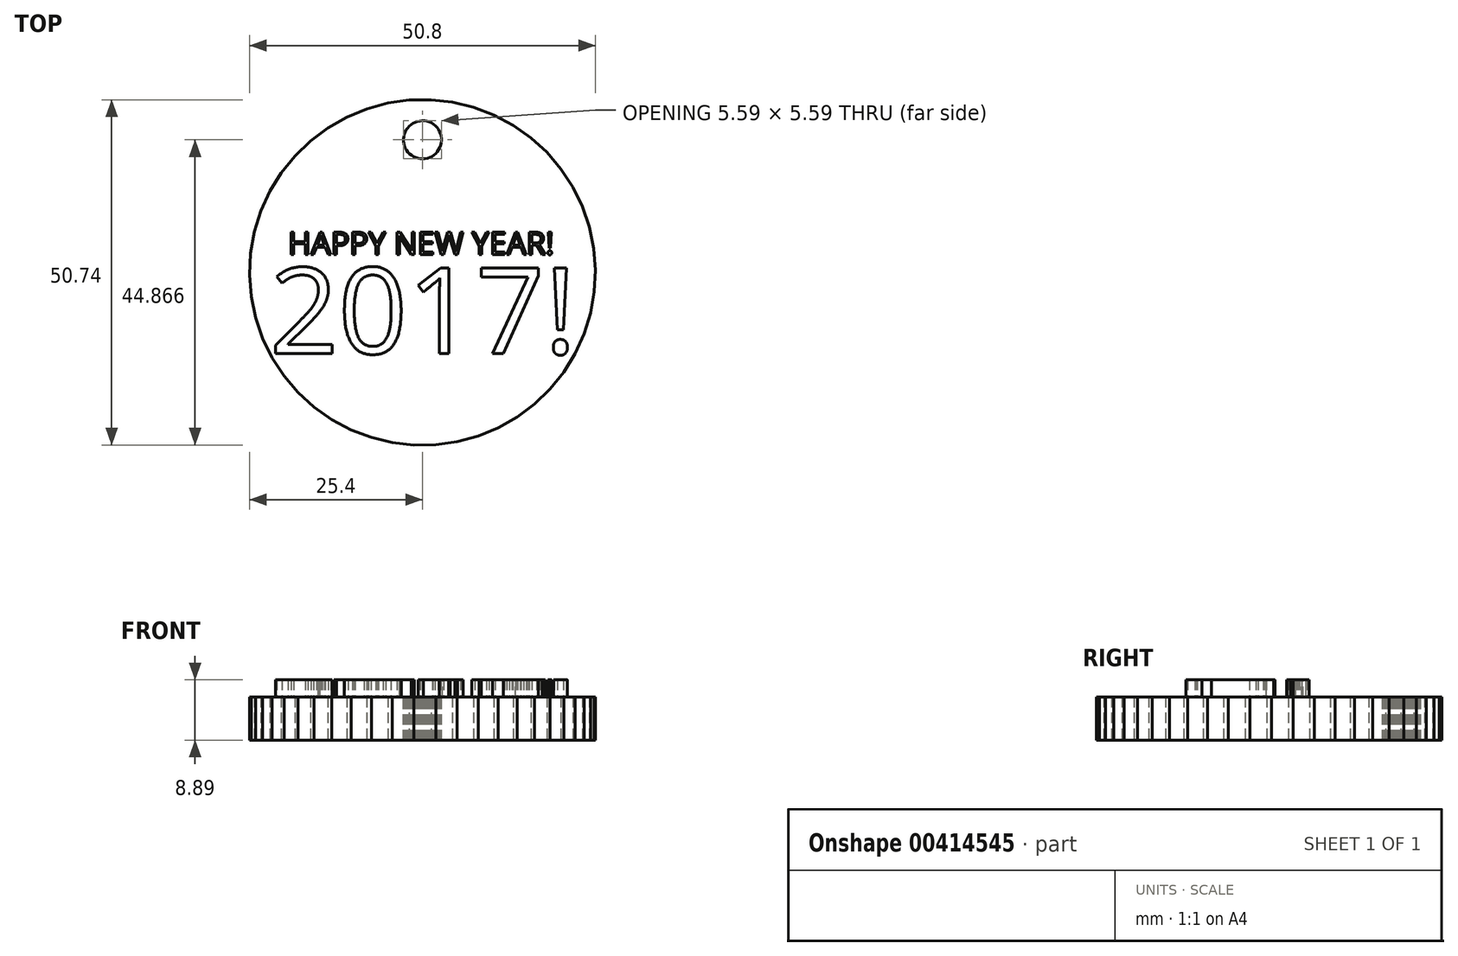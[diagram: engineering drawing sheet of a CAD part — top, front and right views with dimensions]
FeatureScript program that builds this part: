
annotation { "Feature Type Name" : "Feature", "Feature Type Description" : "" }
export const myFeature = defineFeature(function(context is Context, id is Id, definition is map)
    precondition{}
    {
        {
            var Q0;
            Q0=qCreatedBy(makeId("Top.planeOp"),FACE);
            var sketch = newSketch(context, id + "F0", { "sketchPlane" : qUnion([Q0])});
            skCircle(sketch, "E0.cCircle", {"center": v(0, 0) * mm, "radius": 25.4 * mm, "construction": true});
            skLineSegment(sketch, "E0.0", {"start": v(22.09, 12.54) * mm, "end": v(23.48, 9.68) * mm});
            skLineSegment(sketch, "E0.1", {"start": v(23.48, 9.68) * mm, "end": v(24.51, 6.66) * mm});
            skLineSegment(sketch, "E0.2", {"start": v(24.51, 6.66) * mm, "end": v(25.15, 3.53) * mm});
            skLineSegment(sketch, "E0.3", {"start": v(25.15, 3.53) * mm, "end": v(25.4, 0.35) * mm});
            skLineSegment(sketch, "E0.4", {"start": v(25.4, 0.35) * mm, "end": v(25.24, -2.83) * mm});
            skLineSegment(sketch, "E0.5", {"start": v(25.24, -2.83) * mm, "end": v(24.69, -5.98) * mm});
            skLineSegment(sketch, "E0.6", {"start": v(24.69, -5.98) * mm, "end": v(23.74, -9.02) * mm});
            skLineSegment(sketch, "E0.7", {"start": v(23.74, -9.02) * mm, "end": v(22.43, -11.93) * mm});
            skLineSegment(sketch, "E0.8", {"start": v(22.43, -11.93) * mm, "end": v(20.75, -14.64) * mm});
            skLineSegment(sketch, "E0.9", {"start": v(20.75, -14.64) * mm, "end": v(18.75, -17.13) * mm});
            skLineSegment(sketch, "E0.10", {"start": v(18.75, -17.13) * mm, "end": v(16.46, -19.34) * mm});
            skLineSegment(sketch, "E0.11", {"start": v(16.46, -19.34) * mm, "end": v(13.9, -21.26) * mm});
            skLineSegment(sketch, "E0.12", {"start": v(13.9, -21.26) * mm, "end": v(11.13, -22.83) * mm});
            skLineSegment(sketch, "E0.13", {"start": v(11.13, -22.83) * mm, "end": v(8.18, -24.05) * mm});
            skLineSegment(sketch, "E0.14", {"start": v(8.18, -24.05) * mm, "end": v(5.1, -24.88) * mm});
            skLineSegment(sketch, "E0.15", {"start": v(5.1, -24.88) * mm, "end": v(1.95, -25.33) * mm});
            skLineSegment(sketch, "E0.16", {"start": v(1.95, -25.33) * mm, "end": v(-1.24, -25.37) * mm});
            skLineSegment(sketch, "E0.17", {"start": v(-1.24, -25.37) * mm, "end": v(-4.41, -25.01) * mm});
            skLineSegment(sketch, "E0.18", {"start": v(-4.41, -25.01) * mm, "end": v(-7.51, -24.26) * mm});
            skLineSegment(sketch, "E0.19", {"start": v(-7.51, -24.26) * mm, "end": v(-10.5, -23.13) * mm});
            skLineSegment(sketch, "E0.20", {"start": v(-10.5, -23.13) * mm, "end": v(-13.31, -21.63) * mm});
            skLineSegment(sketch, "E0.21", {"start": v(-13.31, -21.63) * mm, "end": v(-15.92, -19.8) * mm});
            skLineSegment(sketch, "E0.22", {"start": v(-15.92, -19.8) * mm, "end": v(-18.27, -17.64) * mm});
            skLineSegment(sketch, "E0.23", {"start": v(-18.27, -17.64) * mm, "end": v(-20.34, -15.21) * mm});
            skLineSegment(sketch, "E0.24", {"start": v(-20.34, -15.21) * mm, "end": v(-22.09, -12.54) * mm});
            skLineSegment(sketch, "E0.25", {"start": v(-22.09, -12.54) * mm, "end": v(-23.48, -9.68) * mm});
            skLineSegment(sketch, "E0.26", {"start": v(-23.48, -9.68) * mm, "end": v(-24.51, -6.66) * mm});
            skLineSegment(sketch, "E0.27", {"start": v(-24.51, -6.66) * mm, "end": v(-25.15, -3.53) * mm});
            skLineSegment(sketch, "E0.28", {"start": v(-25.15, -3.53) * mm, "end": v(-25.4, -0.35) * mm});
            skLineSegment(sketch, "E0.29", {"start": v(-25.4, -0.35) * mm, "end": v(-25.24, 2.83) * mm});
            skLineSegment(sketch, "E0.30", {"start": v(-25.24, 2.83) * mm, "end": v(-24.69, 5.98) * mm});
            skLineSegment(sketch, "E0.31", {"start": v(-24.69, 5.98) * mm, "end": v(-23.74, 9.02) * mm});
            skLineSegment(sketch, "E0.32", {"start": v(-23.74, 9.02) * mm, "end": v(-22.43, 11.93) * mm});
            skLineSegment(sketch, "E0.33", {"start": v(-22.43, 11.93) * mm, "end": v(-20.75, 14.64) * mm});
            skLineSegment(sketch, "E0.34", {"start": v(-20.75, 14.64) * mm, "end": v(-18.75, 17.13) * mm});
            skLineSegment(sketch, "E0.35", {"start": v(-18.75, 17.13) * mm, "end": v(-16.46, 19.34) * mm});
            skLineSegment(sketch, "E0.36", {"start": v(-16.46, 19.34) * mm, "end": v(-13.9, 21.26) * mm});
            skLineSegment(sketch, "E0.37", {"start": v(-13.9, 21.26) * mm, "end": v(-11.13, 22.83) * mm});
            skLineSegment(sketch, "E0.38", {"start": v(-11.13, 22.83) * mm, "end": v(-8.18, 24.05) * mm});
            skLineSegment(sketch, "E0.39", {"start": v(-8.18, 24.05) * mm, "end": v(-5.1, 24.88) * mm});
            skLineSegment(sketch, "E0.40", {"start": v(-5.1, 24.88) * mm, "end": v(-1.95, 25.33) * mm});
            skLineSegment(sketch, "E0.41", {"start": v(-1.95, 25.33) * mm, "end": v(1.24, 25.37) * mm});
            skLineSegment(sketch, "E0.42", {"start": v(1.24, 25.37) * mm, "end": v(4.41, 25.01) * mm});
            skLineSegment(sketch, "E0.43", {"start": v(4.41, 25.01) * mm, "end": v(7.51, 24.26) * mm});
            skLineSegment(sketch, "E0.44", {"start": v(7.51, 24.26) * mm, "end": v(10.5, 23.13) * mm});
            skLineSegment(sketch, "E0.45", {"start": v(10.5, 23.13) * mm, "end": v(13.31, 21.63) * mm});
            skLineSegment(sketch, "E0.46", {"start": v(13.31, 21.63) * mm, "end": v(15.92, 19.8) * mm});
            skLineSegment(sketch, "E0.47", {"start": v(15.92, 19.8) * mm, "end": v(18.27, 17.64) * mm});
            skLineSegment(sketch, "E0.48", {"start": v(18.27, 17.64) * mm, "end": v(20.34, 15.21) * mm});
            skLineSegment(sketch, "E0.49", {"start": v(20.34, 15.21) * mm, "end": v(22.09, 12.54) * mm});
            skSolve(sketch);
        }
        {
            var Q0;
            Q0=makeQuery(id+"F0.imprint","IMPRINT",FACE,{"disambiguationData":[TD([[makeQuery(id+"F0.imprint","IMPRINT",EDGE,{"derivedFrom":sQuery(id+"F0.wireOp",EDGE,"E0.0")}),-1.0]])]});
            extrude(context, id + "F1", {"entities" : qUnion([Q0]), "depth" : 6.35 * mm});
        }
        {
            var Q0;
            Q0=makeQuery(id+"F1.opExtrude","CAP_FACE",FACE,{"disambiguationData":[OSD([sQuery(id+"F0.wireOp",EDGE,"E0.0"),sQuery(id+"F0.wireOp",EDGE,"E0.1"),sQuery(id+"F0.wireOp",EDGE,"E0.2"),sQuery(id+"F0.wireOp",EDGE,"E0.3"),sQuery(id+"F0.wireOp",EDGE,"E0.4"),sQuery(id+"F0.wireOp",EDGE,"E0.5"),sQuery(id+"F0.wireOp",EDGE,"E0.6"),sQuery(id+"F0.wireOp",EDGE,"E0.7"),sQuery(id+"F0.wireOp",EDGE,"E0.8"),sQuery(id+"F0.wireOp",EDGE,"E0.9"),sQuery(id+"F0.wireOp",EDGE,"E0.10"),sQuery(id+"F0.wireOp",EDGE,"E0.11"),sQuery(id+"F0.wireOp",EDGE,"E0.12"),sQuery(id+"F0.wireOp",EDGE,"E0.13"),sQuery(id+"F0.wireOp",EDGE,"E0.14"),sQuery(id+"F0.wireOp",EDGE,"E0.15"),sQuery(id+"F0.wireOp",EDGE,"E0.16"),sQuery(id+"F0.wireOp",EDGE,"E0.17"),sQuery(id+"F0.wireOp",EDGE,"E0.18"),sQuery(id+"F0.wireOp",EDGE,"E0.19"),sQuery(id+"F0.wireOp",EDGE,"E0.20"),sQuery(id+"F0.wireOp",EDGE,"E0.21"),sQuery(id+"F0.wireOp",EDGE,"E0.22"),sQuery(id+"F0.wireOp",EDGE,"E0.23"),sQuery(id+"F0.wireOp",EDGE,"E0.24"),sQuery(id+"F0.wireOp",EDGE,"E0.25"),sQuery(id+"F0.wireOp",EDGE,"E0.26"),sQuery(id+"F0.wireOp",EDGE,"E0.27"),sQuery(id+"F0.wireOp",EDGE,"E0.28"),sQuery(id+"F0.wireOp",EDGE,"E0.29"),sQuery(id+"F0.wireOp",EDGE,"E0.30"),sQuery(id+"F0.wireOp",EDGE,"E0.31"),sQuery(id+"F0.wireOp",EDGE,"E0.32"),sQuery(id+"F0.wireOp",EDGE,"E0.33"),sQuery(id+"F0.wireOp",EDGE,"E0.34"),sQuery(id+"F0.wireOp",EDGE,"E0.35"),sQuery(id+"F0.wireOp",EDGE,"E0.36"),sQuery(id+"F0.wireOp",EDGE,"E0.37"),sQuery(id+"F0.wireOp",EDGE,"E0.38"),sQuery(id+"F0.wireOp",EDGE,"E0.39"),sQuery(id+"F0.wireOp",EDGE,"E0.40"),sQuery(id+"F0.wireOp",EDGE,"E0.41"),sQuery(id+"F0.wireOp",EDGE,"E0.42"),sQuery(id+"F0.wireOp",EDGE,"E0.43"),sQuery(id+"F0.wireOp",EDGE,"E0.44"),sQuery(id+"F0.wireOp",EDGE,"E0.45"),sQuery(id+"F0.wireOp",EDGE,"E0.46"),sQuery(id+"F0.wireOp",EDGE,"E0.47"),sQuery(id+"F0.wireOp",EDGE,"E0.48"),sQuery(id+"F0.wireOp",EDGE,"E0.49")])],"isStart":false});
            var sketch = newSketch(context, id + "F2", { "sketchPlane" : qUnion([Q0])});
            skText(sketch, "E1", { "text": "2017!", "fontName": "OpenSans-Regular.ttf"});
            skPoint(sketch, "E2.firstSnap0", {"position": v(-23.08, 10.47) * mm});
            skText(sketch, "E3", { "text": "HAPPY NEW YEAR!", "fontName": "OpenSans-Regular.ttf"});
            skPoint(sketch, "E3.firstSnap0", {"position": v(-19.75, 15.89) * mm});
            const initialGuessF2  = {"E1": [-0.02243, -0.01193, 1, 0, 0.0127], "E3": [-0.01975, 0.00264, 1, 0, 0.0033]};
            skSetInitialGuess(sketch, initialGuessF2);
            skSolve(sketch);
        }
        {
            var Q0;
            Q0 = qSketchRegion(id + "F2", true);
            extrude(context, id + "F3", {"entities" : qUnion([Q0]), "operationType" : NewBodyOperationType.ADD, "depth" : 2.54 * mm});
        }
        {
            var Q0;
            {var subQ0=sQuery(id+"F0.wireOp",EDGE,"E0.44");var subQ1=sQuery(id+"F0.wireOp",EDGE,"E0.43");var subQ2=sQuery(id+"F0.wireOp",EDGE,"E0.42");var subQ3=sQuery(id+"F0.wireOp",EDGE,"E0.41");var subQ4=sQuery(id+"F0.wireOp",EDGE,"E0.40");var subQ5=sQuery(id+"F0.wireOp",EDGE,"E0.39");var subQ6=sQuery(id+"F0.wireOp",EDGE,"E0.38");var subQ7=sQuery(id+"F0.wireOp",EDGE,"E0.37");var subQ8=sQuery(id+"F0.wireOp",EDGE,"E0.27");var subQ9=sQuery(id+"F0.wireOp",EDGE,"E0.36");var subQ10=sQuery(id+"F0.wireOp",EDGE,"E0.26");var subQ11=sQuery(id+"F0.wireOp",EDGE,"E0.35");var subQ12=sQuery(id+"F0.wireOp",EDGE,"E0.34");var subQ13=sQuery(id+"F0.wireOp",EDGE,"E0.24");var subQ14=sQuery(id+"F0.wireOp",EDGE,"E0.33");var subQ15=sQuery(id+"F0.wireOp",EDGE,"E0.23");var subQ16=sQuery(id+"F0.wireOp",EDGE,"E0.32");var subQ17=sQuery(id+"F0.wireOp",EDGE,"E0.22");var subQ18=sQuery(id+"F0.wireOp",EDGE,"E0.31");var subQ19=sQuery(id+"F0.wireOp",EDGE,"E0.8");var subQ20=sQuery(id+"F0.wireOp",EDGE,"E0.7");var subQ21=sQuery(id+"F0.wireOp",EDGE,"E0.6");var subQ22=sQuery(id+"F0.wireOp",EDGE,"E0.5");var subQ23=sQuery(id+"F0.wireOp",EDGE,"E0.4");var subQ24=sQuery(id+"F0.wireOp",EDGE,"E0.9");var subQ25=sQuery(id+"F0.wireOp",EDGE,"E0.45");var subQ26=sQuery(id+"F0.wireOp",EDGE,"E0.0");var subQ27=sQuery(id+"F0.wireOp",EDGE,"E0.21");var subQ28=sQuery(id+"F0.wireOp",EDGE,"E0.30");var subQ29=sQuery(id+"F0.wireOp",EDGE,"E0.3");var subQ30=sQuery(id+"F0.wireOp",EDGE,"E0.1");var subQ31=sQuery(id+"F0.wireOp",EDGE,"E0.2");var subQ32=sQuery(id+"F0.wireOp",EDGE,"E0.10");var subQ33=sQuery(id+"F0.wireOp",EDGE,"E0.11");var subQ34=sQuery(id+"F0.wireOp",EDGE,"E0.12");var subQ35=sQuery(id+"F0.wireOp",EDGE,"E0.13");var subQ36=sQuery(id+"F0.wireOp",EDGE,"E0.14");var subQ37=sQuery(id+"F0.wireOp",EDGE,"E0.15");var subQ38=sQuery(id+"F0.wireOp",EDGE,"E0.16");var subQ39=sQuery(id+"F0.wireOp",EDGE,"E0.25");var subQ40=sQuery(id+"F0.wireOp",EDGE,"E0.47");var subQ41=sQuery(id+"F0.wireOp",EDGE,"E0.17");var subQ42=sQuery(id+"F0.wireOp",EDGE,"E0.18");var subQ43=sQuery(id+"F0.wireOp",EDGE,"E0.19");var subQ44=sQuery(id+"F0.wireOp",EDGE,"E0.28");var subQ45=sQuery(id+"F0.wireOp",EDGE,"E0.20");var subQ46=sQuery(id+"F0.wireOp",EDGE,"E0.29");var subQ47=sQuery(id+"F0.wireOp",EDGE,"E0.46");var subQ48=sQuery(id+"F0.wireOp",EDGE,"E0.48");var subQ49=sQuery(id+"F0.wireOp",EDGE,"E0.49");Q0=makeQuery(id+"F3.boolean.opBoolean","SPLIT",FACE,{"disambiguationData":[TD([makeQuery(id+"F1.opExtrude","SWEPT_FACE",FACE,{"disambiguationData":[OSD([subQ26])]})])],"derivedFrom":makeQuery(id+"F1.opExtrude","CAP_FACE",FACE,{"disambiguationData":[OSD([subQ26,subQ30,subQ31,subQ29,subQ23,subQ22,subQ21,subQ20,subQ19,subQ24,subQ32,subQ33,subQ34,subQ35,subQ36,subQ37,subQ38,subQ41,subQ42,subQ43,subQ45,subQ27,subQ17,subQ15,subQ13,subQ39,subQ10,subQ8,subQ44,subQ46,subQ28,subQ18,subQ16,subQ14,subQ12,subQ11,subQ9,subQ7,subQ6,subQ5,subQ4,subQ3,subQ2,subQ1,subQ0,subQ25,subQ47,subQ40,subQ48,subQ49])],"isStart":false})});}
            var sketch = newSketch(context, id + "F4", { "sketchPlane" : qUnion([Q0])});
            skCircle(sketch, "E4.cCircle", {"center": v(0, 19.5) * mm, "radius": 2.8 * mm, "construction": true});
            skLineSegment(sketch, "E4.0", {"start": v(2.34, 21.03) * mm, "end": v(2.51, 20.72) * mm});
            skLineSegment(sketch, "E4.1", {"start": v(2.51, 20.72) * mm, "end": v(2.65, 20.4) * mm});
            skLineSegment(sketch, "E4.2", {"start": v(2.65, 20.4) * mm, "end": v(2.74, 20.06) * mm});
            skLineSegment(sketch, "E4.3", {"start": v(2.74, 20.06) * mm, "end": v(2.79, 19.71) * mm});
            skLineSegment(sketch, "E4.4", {"start": v(2.79, 19.71) * mm, "end": v(2.8, 19.36) * mm});
            skLineSegment(sketch, "E4.5", {"start": v(2.8, 19.36) * mm, "end": v(2.75, 19.01) * mm});
            skLineSegment(sketch, "E4.6", {"start": v(2.75, 19.01) * mm, "end": v(2.67, 18.67) * mm});
            skLineSegment(sketch, "E4.7", {"start": v(2.67, 18.67) * mm, "end": v(2.55, 18.34) * mm});
            skLineSegment(sketch, "E4.8", {"start": v(2.55, 18.34) * mm, "end": v(2.38, 18.03) * mm});
            skLineSegment(sketch, "E4.9", {"start": v(2.38, 18.03) * mm, "end": v(2.18, 17.74) * mm});
            skLineSegment(sketch, "E4.10", {"start": v(2.18, 17.74) * mm, "end": v(1.94, 17.48) * mm});
            skLineSegment(sketch, "E4.11", {"start": v(1.94, 17.48) * mm, "end": v(1.68, 17.26) * mm});
            skLineSegment(sketch, "E4.12", {"start": v(1.68, 17.26) * mm, "end": v(1.38, 17.06) * mm});
            skLineSegment(sketch, "E4.13", {"start": v(1.38, 17.06) * mm, "end": v(1.07, 16.91) * mm});
            skLineSegment(sketch, "E4.14", {"start": v(1.07, 16.91) * mm, "end": v(0.73, 16.8) * mm});
            skLineSegment(sketch, "E4.15", {"start": v(0.73, 16.8) * mm, "end": v(0.39, 16.73) * mm});
            skLineSegment(sketch, "E4.16", {"start": v(0.39, 16.73) * mm, "end": v(0.04, 16.7) * mm});
            skLineSegment(sketch, "E4.17", {"start": v(0.04, 16.7) * mm, "end": v(-0.31, 16.72) * mm});
            skLineSegment(sketch, "E4.18", {"start": v(-0.31, 16.72) * mm, "end": v(-0.66, 16.78) * mm});
            skLineSegment(sketch, "E4.19", {"start": v(-0.66, 16.78) * mm, "end": v(-1, 16.88) * mm});
            skLineSegment(sketch, "E4.20", {"start": v(-1, 16.88) * mm, "end": v(-1.31, 17.03) * mm});
            skLineSegment(sketch, "E4.21", {"start": v(-1.31, 17.03) * mm, "end": v(-1.61, 17.21) * mm});
            skLineSegment(sketch, "E4.22", {"start": v(-1.61, 17.21) * mm, "end": v(-1.89, 17.43) * mm});
            skLineSegment(sketch, "E4.23", {"start": v(-1.89, 17.43) * mm, "end": v(-2.13, 17.68) * mm});
            skLineSegment(sketch, "E4.24", {"start": v(-2.13, 17.68) * mm, "end": v(-2.34, 17.96) * mm});
            skLineSegment(sketch, "E4.25", {"start": v(-2.34, 17.96) * mm, "end": v(-2.51, 18.27) * mm});
            skLineSegment(sketch, "E4.26", {"start": v(-2.51, 18.27) * mm, "end": v(-2.65, 18.6) * mm});
            skLineSegment(sketch, "E4.27", {"start": v(-2.65, 18.6) * mm, "end": v(-2.74, 18.93) * mm});
            skLineSegment(sketch, "E4.28", {"start": v(-2.74, 18.93) * mm, "end": v(-2.79, 19.28) * mm});
            skLineSegment(sketch, "E4.29", {"start": v(-2.79, 19.28) * mm, "end": v(-2.8, 19.63) * mm});
            skLineSegment(sketch, "E4.30", {"start": v(-2.8, 19.63) * mm, "end": v(-2.75, 19.98) * mm});
            skLineSegment(sketch, "E4.31", {"start": v(-2.75, 19.98) * mm, "end": v(-2.67, 20.32) * mm});
            skLineSegment(sketch, "E4.32", {"start": v(-2.67, 20.32) * mm, "end": v(-2.55, 20.65) * mm});
            skLineSegment(sketch, "E4.33", {"start": v(-2.55, 20.65) * mm, "end": v(-2.38, 20.96) * mm});
            skLineSegment(sketch, "E4.34", {"start": v(-2.38, 20.96) * mm, "end": v(-2.18, 21.25) * mm});
            skLineSegment(sketch, "E4.35", {"start": v(-2.18, 21.25) * mm, "end": v(-1.94, 21.5) * mm});
            skLineSegment(sketch, "E4.36", {"start": v(-1.94, 21.5) * mm, "end": v(-1.68, 21.74) * mm});
            skLineSegment(sketch, "E4.37", {"start": v(-1.68, 21.74) * mm, "end": v(-1.38, 21.93) * mm});
            skLineSegment(sketch, "E4.38", {"start": v(-1.38, 21.93) * mm, "end": v(-1.07, 22.08) * mm});
            skLineSegment(sketch, "E4.39", {"start": v(-1.07, 22.08) * mm, "end": v(-0.73, 22.2) * mm});
            skLineSegment(sketch, "E4.40", {"start": v(-0.73, 22.2) * mm, "end": v(-0.39, 22.27) * mm});
            skLineSegment(sketch, "E4.41", {"start": v(-0.39, 22.27) * mm, "end": v(-0.04, 22.3) * mm});
            skLineSegment(sketch, "E4.42", {"start": v(-0.04, 22.3) * mm, "end": v(0.31, 22.28) * mm});
            skLineSegment(sketch, "E4.43", {"start": v(0.31, 22.28) * mm, "end": v(0.66, 22.22) * mm});
            skLineSegment(sketch, "E4.44", {"start": v(0.66, 22.22) * mm, "end": v(1, 22.11) * mm});
            skLineSegment(sketch, "E4.45", {"start": v(1, 22.11) * mm, "end": v(1.31, 21.97) * mm});
            skLineSegment(sketch, "E4.46", {"start": v(1.31, 21.97) * mm, "end": v(1.61, 21.78) * mm});
            skLineSegment(sketch, "E4.47", {"start": v(1.61, 21.78) * mm, "end": v(1.89, 21.56) * mm});
            skLineSegment(sketch, "E4.48", {"start": v(1.89, 21.56) * mm, "end": v(2.13, 21.3) * mm});
            skLineSegment(sketch, "E4.49", {"start": v(2.13, 21.3) * mm, "end": v(2.34, 21.03) * mm});
            skSolve(sketch);
        }
        {
            var Q0;
            Q0=makeQuery(id+"F4.imprint","IMPRINT",FACE,{"disambiguationData":[TD([[makeQuery(id+"F4.imprint","IMPRINT",EDGE,{"derivedFrom":sQuery(id+"F4.wireOp",EDGE,"E4.0")}),-1.0]])]});
            extrude(context, id + "F5", {"entities" : qUnion([Q0]), "operationType" : NewBodyOperationType.REMOVE, "oppositeDirection" : true, "depth" : 25.4 * mm});
        }
    });
